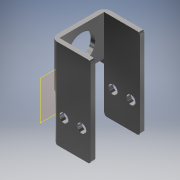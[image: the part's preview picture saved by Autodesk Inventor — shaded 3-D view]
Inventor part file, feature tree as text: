
AUTODESK INVENTOR PART (.ipt)
format: ipt  version: 2017 (Build 210142000, 142)  size: 195,584 bytes
history: native  units: in
note: dims shown in document units (in); Inventor stores cm internally (conversion verified against a paired STEP export)
features: fillet x6, sketch x5, extrude x5, plane x1
ambient origin geometry x8: Origin, YZ Plane, XZ Plane, XY Plane, X Axis, Y Axis, Z Axis, Center Point
bodies: Solid1 (feature_tree)
feature tree (17):
  sketch  "Sketch1"  dims[d0=1.0in d1=1.0in]
  plane  "Work Plane2"
  extrude  "Extrusion2"  Depth=1.0in
  extrude  "Extrusion3"  Depth=0.1in
  extrude  "Extrusion4"  Depth=1.0in
  fillet  "Fillet1"  Radius=1.0in
  fillet  "Fillet2"  Radius=0.8in
  fillet  "Fillet3"  Radius=0.1in
  fillet  "Fillet4"  Radius=1.5875in
  fillet  "Fillet5"  Radius=0.0625in
  fillet  "Fillet6"  Radius=0.0625in
  extrude  "Extrusion5"  Depth=0.0625in
  extrude  "Extrusion6"  Depth=0.15in
  sketch  "Sketch2"  dims[d2=0.1in d3=0.1in]
  sketch  "Sketch3"  dims[d10=0.1in d11=1.0in d12=1.0in d13=0.8in d14=0.0in d18=0.1in d19=0.0in d25=1.5875in d26=0.0in d27=0.0625in d28=0.0625in]
  sketch  "Sketch4"  dims[d29=0.0625in d30=0.0625in]
  sketch  "Sketch5"  dims[d31=0.0625in d32=0.15in d33=0.1in d34=0.0in d35=0.1875in d36=1.525in d37=0.0in]
